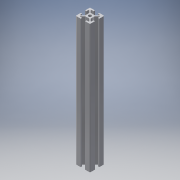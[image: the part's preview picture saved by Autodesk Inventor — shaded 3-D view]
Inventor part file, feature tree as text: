
AUTODESK INVENTOR PART (.ipt)
format: ipt  version: 2016 (Build 200138000, 138)  size: 224,768 bytes
history: native  units: mm
features: other x7, sketch x2, extrude x1, hole x1
ambient origin geometry x8: Origin, YZ Plane, XZ Plane, XY Plane, X Axis, Y Axis, Z Axis, Center Point
bodies: Solid1 (feature_tree)
feature tree (11):
  extrude  "Extrusion1"  TaperAngle=0.0deg  [1 undecoded]
  hole  "Hole1"  [1 undecoded]
  other  "C1_XY"
  other  "C1_YZ"
  other  "C1_ZX"
  other  "C1_X"
  other  "C1_Y"
  other  "C1_Z"
  other  "C1_Center"
  sketch  "Sketch_75"  dims[d2=4.2mm d3=6.0mm d4=4.0mm d5=2.0mm d6=90.0deg d7=200.0mm d8=0.0mm d9=0.0mm]
  sketch  "Sketch2"  dims[d0=180.0mm d1=0.0mm]
note: 2 required parameter values undecoded (feature->parameter linkage not recoverable at this tier; creation-order binding heuristic only, values carry confidence <= 0.55)
